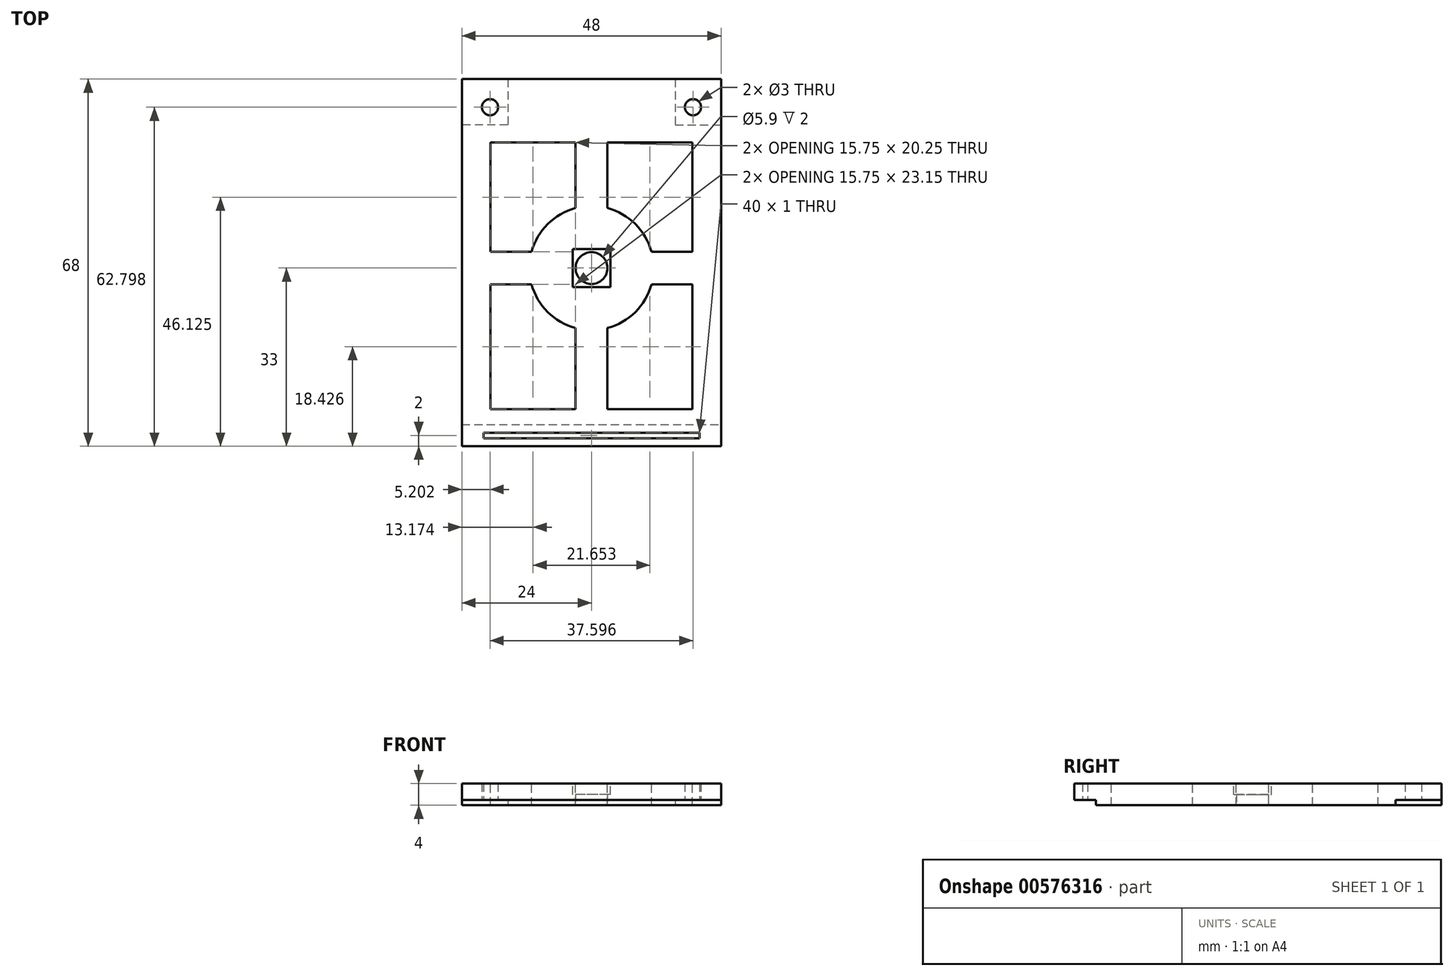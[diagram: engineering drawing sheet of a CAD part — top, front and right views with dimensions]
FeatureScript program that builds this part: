
annotation { "Feature Type Name" : "Feature", "Feature Type Description" : "" }
export const myFeature = defineFeature(function(context is Context, id is Id, definition is map)
    precondition{}
    {
        {
            var Q0;
            Q0=qCreatedBy(makeId("Top.planeOp"),FACE);
            var sketch = newSketch(context, id + "F0", { "sketchPlane" : qUnion([Q0])});
            skLineSegment(sketch, "E0.bottom", {"start": v(24, -33) * mm, "end": v(-24, -33) * mm});
            skLineSegment(sketch, "E0.top", {"start": v(17.5, 35) * mm, "end": v(-17.5, 35) * mm});
            skLineSegment(sketch, "E0.left", {"start": v(24, -33) * mm, "end": v(24, 26.5) * mm});
            skLineSegment(sketch, "E0.right", {"start": v(-24, -33) * mm, "end": v(-24, 26.5) * mm});
            skPoint(sketch, "E0.middle", {"position": v(0, 0) * mm});
            skCircle(sketch, "E1", {"center": v(0, 0) * mm, "radius": 2.95 * mm});
            skLineSegment(sketch, "E2", {"start": v(-24, 35) * mm, "end": v(-24, 26.5) * mm});
            skLineSegment(sketch, "E3", {"start": v(-17.5, 35) * mm, "end": v(-24, 35) * mm});
            skLineSegment(sketch, "E4", {"start": v(17.5, 35) * mm, "end": v(24, 35) * mm});
            skLineSegment(sketch, "E5", {"start": v(24, 26.5) * mm, "end": v(24, 35) * mm});
            skSolve(sketch);
        }
        {
            var Q0;
            Q0 = qSketchRegion(id + "F0", true);
            extrude(context, id + "F1", {"entities" : qUnion([Q0]), "depth" : 4 * mm, "offsetDistance" : 25 * mm});
        }
        {
            var Q0;
            Q0=makeQuery(id+"F1.opExtrude","CAP_FACE",FACE,{"disambiguationData":[OSD([sQuery(id+"F0.wireOp",EDGE,"E0.bottom"),sQuery(id+"F0.wireOp",EDGE,"E0.top"),sQuery(id+"F0.wireOp",EDGE,"E0.left"),sQuery(id+"F0.wireOp",EDGE,"E0.right"),sQuery(id+"F0.wireOp",EDGE,"fb62c716-a95b-4c36-b64f-addef10a23f3.filletArc"),sQuery(id+"F0.wireOp",EDGE,"5cd2d900-9a19-4462-aa59-3719ee29f727.filletArc"),sQuery(id+"F0.wireOp",EDGE,"E1")])],"isStart":true});
            var sketch = newSketch(context, id + "F2", { "sketchPlane" : qUnion([Q0])});
            skLineSegment(sketch, "E6", {"start": v(15.5, -35) * mm, "end": v(15.5, -26.5) * mm});
            skLineSegment(sketch, "E7", {"start": v(15.5, -26.5) * mm, "end": v(24, -26.5) * mm});
            skLineSegment(sketch, "E8", {"start": v(-15.5, -35) * mm, "end": v(-15.5, -26.5) * mm});
            skLineSegment(sketch, "E9", {"start": v(-15.5, -26.5) * mm, "end": v(-24, -26.5) * mm});
            skSolve(sketch);
        }
        {
            var Q0;
            {var subQ2=sQuery(id+"F2.wireOp",EDGE,"E6");Q0=makeQuery(id+"F2.imprint","IMPRINT",FACE,{"disambiguationData":[TD([[makeQuery(id+"F2.imprint","IMPRINT",EDGE,{"derivedFrom":subQ2}),-1.0]])]});}
            var Q1;
            {var subQ2=sQuery(id+"F2.wireOp",EDGE,"E8");Q1=makeQuery(id+"F2.imprint","IMPRINT",FACE,{"disambiguationData":[TD([[makeQuery(id+"F2.imprint","IMPRINT",EDGE,{"derivedFrom":subQ2}),1.0]])]});}
            extrude(context, id + "F3", {"entities" : qUnion([Q0, Q1]), "operationType" : NewBodyOperationType.REMOVE, "oppositeDirection" : true, "depth" : 1 * mm, "offsetDistance" : 25 * mm});
        }
        {
            var Q0;
            Q0=makeQuery(id+"F3.boolean.opBoolean","COPY",FACE,{"derivedFrom":makeQuery(id+"F3.opExtrude","CAP_FACE",FACE,{"disambiguationData":[OSD([sQuery(id+"F0.wireOp",EDGE,"E0.top"),sQuery(id+"F0.wireOp",EDGE,"E0.left"),sQuery(id+"F0.wireOp",EDGE,"5cd2d900-9a19-4462-aa59-3719ee29f727.filletArc"),sQuery(id+"F2.wireOp",EDGE,"E6"),sQuery(id+"F2.wireOp",EDGE,"E7")])],"isStart":false})});
            var sketch = newSketch(context, id + "F4", { "sketchPlane" : qUnion([Q0])});
            skCircle(sketch, "E10", {"center": v(18.8, -29.8) * mm, "radius": 1.5 * mm});
            skSolve(sketch);
        }
        {
            var Q0;
            Q0 = qSketchRegion(id + "F4", true);
            extrude(context, id + "F5", {"entities" : qUnion([Q0]), "operationType" : NewBodyOperationType.REMOVE, "oppositeDirection" : true, "depth" : 3 * mm, "offsetDistance" : 25 * mm});
        }
        {
            var Q0;
            Q0=makeQuery(id+"F1.opExtrude","CAP_FACE",FACE,{"disambiguationData":[OSD([sQuery(id+"F0.wireOp",EDGE,"E0.bottom"),sQuery(id+"F0.wireOp",EDGE,"E0.top"),sQuery(id+"F0.wireOp",EDGE,"E0.left"),sQuery(id+"F0.wireOp",EDGE,"E0.right"),sQuery(id+"F0.wireOp",EDGE,"fb62c716-a95b-4c36-b64f-addef10a23f3.filletArc"),sQuery(id+"F0.wireOp",EDGE,"5cd2d900-9a19-4462-aa59-3719ee29f727.filletArc"),sQuery(id+"F0.wireOp",EDGE,"E1")])],"isStart":false});
            var sketch = newSketch(context, id + "F6", { "sketchPlane" : qUnion([Q0])});
            skLineSegment(sketch, "E11", {"start": v(-18.7, -16.13) * mm, "end": v(-18.7, -9.13) * mm});
            skLineSegment(sketch, "E12", {"start": v(18.7, -16.13) * mm, "end": v(18.7, -9.13) * mm});
            skCircle(sketch, "E13", {"center": v(0, 0) * mm, "radius": 11.5 * mm});
            skLineSegment(sketch, "E14", {"start": v(-11.1, -3) * mm, "end": v(11.1, -3) * mm, "construction": true});
            skLineSegment(sketch, "E15", {"start": v(-11.1, 3) * mm, "end": v(11.1, 3) * mm, "construction": true});
            skLineSegment(sketch, "E16", {"start": v(18.7, -9.13) * mm, "end": v(18.7, -3.9) * mm});
            skLineSegment(sketch, "E17", {"start": v(11.1, -3) * mm, "end": v(18.7, -3) * mm});
            skLineSegment(sketch, "E18", {"start": v(18.7, -3.9) * mm, "end": v(18.7, -3) * mm});
            skLineSegment(sketch, "E19", {"start": v(-11.1, -3) * mm, "end": v(-17.73, -3) * mm});
            skLineSegment(sketch, "E20", {"start": v(-18.7, -9.13) * mm, "end": v(-18.7, -3) * mm});
            skLineSegment(sketch, "E21", {"start": v(-17.73, -3) * mm, "end": v(-18.7, -3) * mm});
            skLineSegment(sketch, "E22", {"start": v(-11.1, 3) * mm, "end": v(-18.7, 3) * mm});
            skLineSegment(sketch, "E23", {"start": v(11.1, 3) * mm, "end": v(18.7, 3) * mm});
            skLineSegment(sketch, "E24", {"start": v(18.7, 23.25) * mm, "end": v(18.7, 3) * mm});
            skLineSegment(sketch, "E25", {"start": v(-18.7, 23.25) * mm, "end": v(-18.7, 3) * mm});
            skLineSegment(sketch, "E26", {"start": v(-18.7, 23.25) * mm, "end": v(18.7, 23.25) * mm, "construction": true});
            skLineSegment(sketch, "E27", {"start": v(-2.95, -26.15) * mm, "end": v(-2.95, 23.25) * mm});
            skLineSegment(sketch, "E28", {"start": v(2.95, 23.25) * mm, "end": v(2.95, -26.15) * mm});
            skLineSegment(sketch, "E29", {"start": v(-18.7, 23.25) * mm, "end": v(-2.95, 23.25) * mm});
            skLineSegment(sketch, "E30", {"start": v(2.95, 23.25) * mm, "end": v(18.7, 23.25) * mm});
            skLineSegment(sketch, "E31", {"start": v(-10, -26.15) * mm, "end": v(-2.95, -26.15) * mm});
            skLineSegment(sketch, "E32", {"start": v(2.95, -26.15) * mm, "end": v(10, -26.15) * mm});
            skLineSegment(sketch, "E33", {"start": v(-10, -26.15) * mm, "end": v(-18.7, -26.15) * mm});
            skLineSegment(sketch, "E34", {"start": v(-18.7, -16.13) * mm, "end": v(-18.7, -26.15) * mm});
            skLineSegment(sketch, "E35", {"start": v(10, -26.15) * mm, "end": v(18.7, -26.15) * mm});
            skLineSegment(sketch, "E36", {"start": v(18.7, -16.13) * mm, "end": v(18.7, -26.15) * mm});
            skSolve(sketch);
        }
        {
            var Q0;
            {var subQ1=sQuery(id+"F6.wireOp",EDGE,"E22");Q0=makeQuery(id+"F6.imprint","IMPRINT",FACE,{"disambiguationData":[TD([[makeQuery(id+"F6.imprint","IMPRINT",EDGE,{"derivedFrom":subQ1}),-1.0]])]});}
            var Q1;
            Q1=makeQuery(id+"F6.imprint","IMPRINT",FACE,{"disambiguationData":[TD([[makeQuery(id+"F6.imprint","IMPRINT",EDGE,{"derivedFrom":sQuery(id+"F6.wireOp",EDGE,"bOecCgaA-y46j-5zpw-tGMs-dQpOtJMMZCtV")}),1.0]])]});
            var Q2;
            {var subQ4=sQuery(id+"F6.wireOp",EDGE,"E23");Q2=makeQuery(id+"F6.imprint","IMPRINT",FACE,{"disambiguationData":[TD([[makeQuery(id+"F6.imprint","IMPRINT",EDGE,{"derivedFrom":subQ4}),1.0]])]});}
            var Q3;
            Q3=makeQuery(id+"F6.imprint","IMPRINT",FACE,{"disambiguationData":[TD([[makeQuery(id+"F6.imprint","IMPRINT",EDGE,{"derivedFrom":sQuery(id+"F6.wireOp",EDGE,"DgyjjRne-ViLY-uyha-XKUh-3UpNuqNASm8V")}),1.0]])]});
            var Q4;
            Q4=makeQuery(id+"F6.imprint","IMPRINT",FACE,{"disambiguationData":[TD([[makeQuery(id+"F6.imprint","IMPRINT",EDGE,{"derivedFrom":sQuery(id+"F6.wireOp",EDGE,"E11")}),-1.0]])]});
            var Q5;
            Q5=makeQuery(id+"F6.imprint","IMPRINT",FACE,{"disambiguationData":[TD([[makeQuery(id+"F6.imprint","IMPRINT",EDGE,{"derivedFrom":sQuery(id+"F6.wireOp",EDGE,"E12")}),1.0]])]});
            extrude(context, id + "F7", {"entities" : qUnion([Q0, Q1, Q2, Q3, Q4, Q5]), "operationType" : NewBodyOperationType.REMOVE, "oppositeDirection" : true, "depth" : 4 * mm, "offsetDistance" : 25 * mm});
        }
        {
            var Q0;
            Q0=makeQuery(id+"F3.boolean.opBoolean","COPY",FACE,{"derivedFrom":makeQuery(id+"F3.opExtrude","CAP_FACE",FACE,{"disambiguationData":[OSD([sQuery(id+"F0.wireOp",EDGE,"E0.top"),sQuery(id+"F0.wireOp",EDGE,"E0.right"),sQuery(id+"F0.wireOp",EDGE,"fb62c716-a95b-4c36-b64f-addef10a23f3.filletArc"),sQuery(id+"F2.wireOp",EDGE,"E8"),sQuery(id+"F2.wireOp",EDGE,"E9")])],"isStart":false})});
            var sketch = newSketch(context, id + "F8", { "sketchPlane" : qUnion([Q0])});
            skCircle(sketch, "E37", {"center": v(-18.8, -29.8) * mm, "radius": 1.5 * mm});
            skSolve(sketch);
        }
        {
            var Q0;
            Q0=makeQuery(id+"F8.imprint","IMPRINT",FACE,{"disambiguationData":[TD([[makeQuery(id+"F8.imprint","IMPRINT",EDGE,{"derivedFrom":sQuery(id+"F8.wireOp",EDGE,"E37")}),1.0]])]});
            extrude(context, id + "F9", {"entities" : qUnion([Q0]), "operationType" : NewBodyOperationType.REMOVE, "oppositeDirection" : true, "depth" : 3 * mm, "offsetDistance" : 25 * mm});
        }
        {
            var Q0;
            Q0=makeQuery(id+"F1.opExtrude","CAP_FACE",FACE,{"disambiguationData":[OSD([sQuery(id+"F0.wireOp",EDGE,"E0.bottom"),sQuery(id+"F0.wireOp",EDGE,"E0.top"),sQuery(id+"F0.wireOp",EDGE,"E0.left"),sQuery(id+"F0.wireOp",EDGE,"E0.right"),sQuery(id+"F0.wireOp",EDGE,"E1"),sQuery(id+"F0.wireOp",EDGE,"E2"),sQuery(id+"F0.wireOp",EDGE,"E3"),sQuery(id+"F0.wireOp",EDGE,"E4"),sQuery(id+"F0.wireOp",EDGE,"E5")])],"isStart":true});
            var sketch = newSketch(context, id + "F10", { "sketchPlane" : qUnion([Q0])});
            skLineSegment(sketch, "E38", {"start": v(-24, 29) * mm, "end": v(24, 29) * mm});
            skSolve(sketch);
        }
        {
            var Q0;
            {var subQ0=sQuery(id+"F10.wireOp",EDGE,"E38");Q0=makeQuery(id+"F10.imprint","IMPRINT",FACE,{"disambiguationData":[TD([[makeQuery(id+"F10.imprint","IMPRINT",EDGE,{"derivedFrom":subQ0}),1.0]])]});}
            extrude(context, id + "F11", {"entities" : qUnion([Q0]), "operationType" : NewBodyOperationType.REMOVE, "oppositeDirection" : true, "depth" : 1 * mm, "offsetDistance" : 25 * mm});
        }
        {
            var Q0;
            Q0=makeQuery(id+"F11.boolean.opBoolean","COPY",FACE,{"derivedFrom":makeQuery(id+"F11.opExtrude","CAP_FACE",FACE,{"disambiguationData":[OSD([sQuery(id+"F0.wireOp",EDGE,"E0.bottom"),sQuery(id+"F0.wireOp",EDGE,"E0.left"),sQuery(id+"F0.wireOp",EDGE,"E0.right"),sQuery(id+"F0.wireOp",EDGE,"E2"),sQuery(id+"F0.wireOp",EDGE,"E5"),sQuery(id+"F10.wireOp",EDGE,"E38")])],"isStart":false})});
            var sketch = newSketch(context, id + "F12", { "sketchPlane" : qUnion([Q0])});
            skLineSegment(sketch, "E39.bottom", {"start": v(20, 30.5) * mm, "end": v(-20, 30.5) * mm});
            skLineSegment(sketch, "E39.top", {"start": v(20, 31.5) * mm, "end": v(-20, 31.5) * mm});
            skLineSegment(sketch, "E39.left", {"start": v(20, 30.5) * mm, "end": v(20, 31.5) * mm});
            skLineSegment(sketch, "E39.right", {"start": v(-20, 30.5) * mm, "end": v(-20, 31.5) * mm});
            skPoint(sketch, "E39.middle", {"position": v(0, 31) * mm});
            skSolve(sketch);
        }
        {
            var Q0;
            Q0=makeQuery(id+"F12.imprint","IMPRINT",FACE,{"disambiguationData":[TD([[makeQuery(id+"F12.imprint","IMPRINT",EDGE,{"derivedFrom":sQuery(id+"F12.wireOp",EDGE,"E39.bottom")}),-1.0]])]});
            extrude(context, id + "F13", {"entities" : qUnion([Q0]), "operationType" : NewBodyOperationType.REMOVE, "oppositeDirection" : true, "depth" : 3 * mm, "offsetDistance" : 25 * mm});
        }
        {
            var Q0;
            Q0=makeQuery(id+"F1.opExtrude","CAP_FACE",FACE,{"disambiguationData":[OSD([sQuery(id+"F0.wireOp",EDGE,"E0.bottom"),sQuery(id+"F0.wireOp",EDGE,"E0.top"),sQuery(id+"F0.wireOp",EDGE,"E0.left"),sQuery(id+"F0.wireOp",EDGE,"E0.right"),sQuery(id+"F0.wireOp",EDGE,"E1"),sQuery(id+"F0.wireOp",EDGE,"E2"),sQuery(id+"F0.wireOp",EDGE,"E3"),sQuery(id+"F0.wireOp",EDGE,"E4"),sQuery(id+"F0.wireOp",EDGE,"E5")])],"isStart":false});
            var sketch = newSketch(context, id + "F14", { "sketchPlane" : qUnion([Q0])});
            skLineSegment(sketch, "E40.bottom", {"start": v(3.5, -3.5) * mm, "end": v(-3.5, -3.5) * mm});
            skLineSegment(sketch, "E40.top", {"start": v(3.5, 3.5) * mm, "end": v(-3.5, 3.5) * mm});
            skLineSegment(sketch, "E40.left", {"start": v(3.5, -3.5) * mm, "end": v(3.5, 3.5) * mm});
            skLineSegment(sketch, "E40.right", {"start": v(-3.5, -3.5) * mm, "end": v(-3.5, 3.5) * mm});
            skPoint(sketch, "E40.middle", {"position": v(0, 0) * mm});
            skSolve(sketch);
        }
        {
            var Q0;
            Q0=makeQuery(id+"F14.imprint","IMPRINT",FACE,{"disambiguationData":[TD([[makeQuery(id+"F14.imprint","IMPRINT",EDGE,{"derivedFrom":sQuery(id+"F14.wireOp",EDGE,"E40.bottom")}),-1.0]])]});
            extrude(context, id + "F15", {"entities" : qUnion([Q0]), "operationType" : NewBodyOperationType.REMOVE, "oppositeDirection" : true, "depth" : 2 * mm, "offsetDistance" : 25 * mm});
        }
    });
